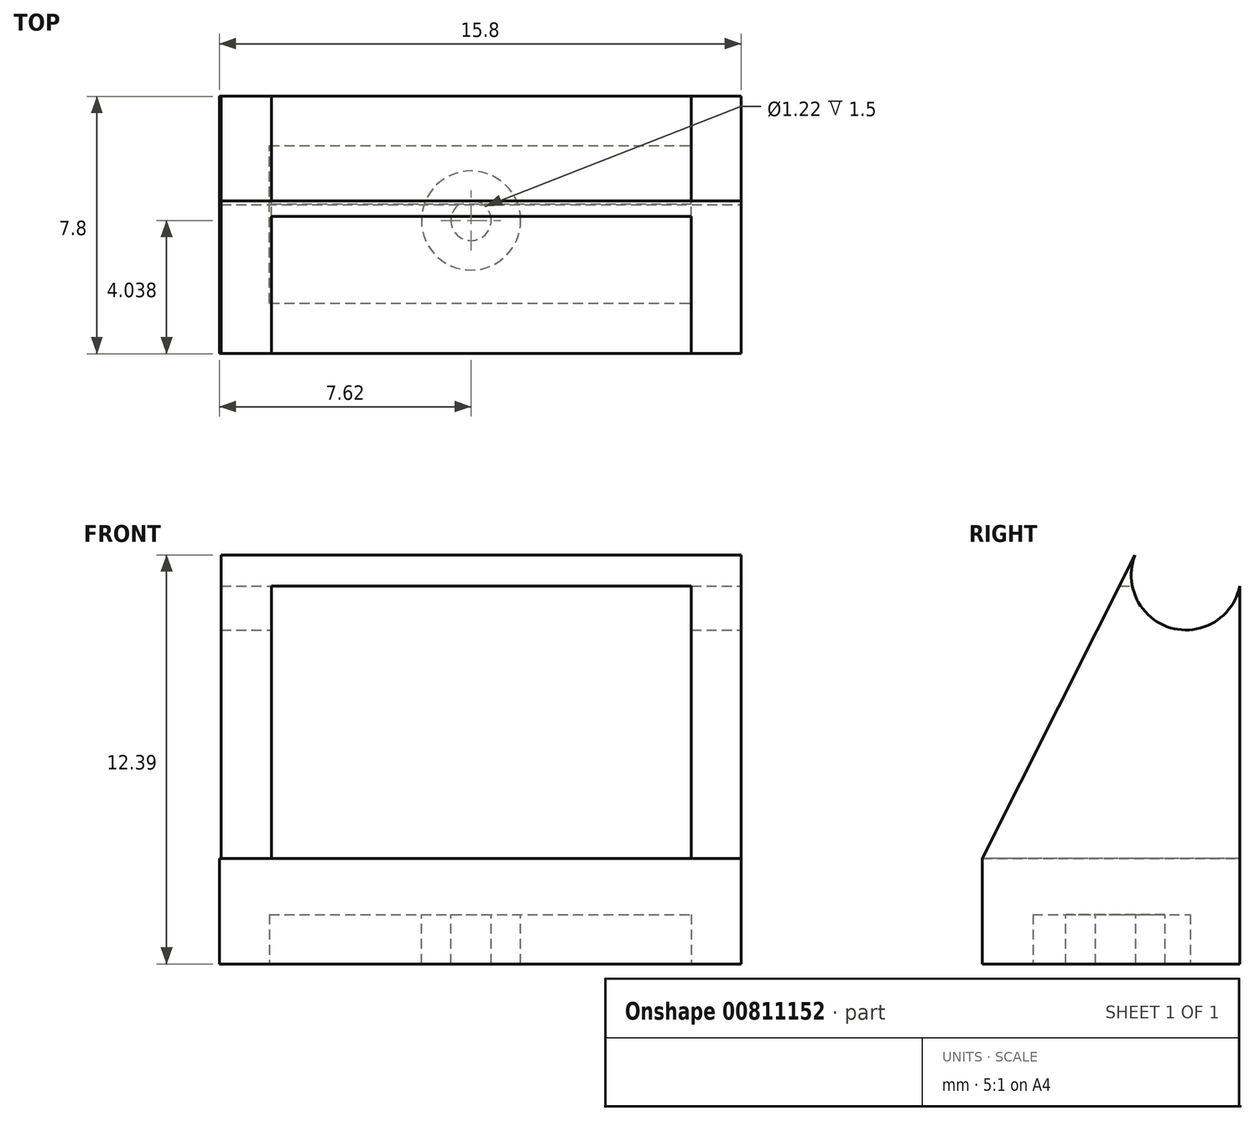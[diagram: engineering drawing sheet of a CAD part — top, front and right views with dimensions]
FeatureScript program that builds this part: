
annotation { "Feature Type Name" : "Feature", "Feature Type Description" : "" }
export const myFeature = defineFeature(function(context is Context, id is Id, definition is map)
    precondition{}
    {
        {
            var Q0;
            Q0=qCreatedBy(makeId("Top.planeOp"),FACE);
            var sketch = newSketch(context, id + "F0", { "sketchPlane" : qUnion([Q0])});
            skLineSegment(sketch, "E0.bottom", {"start": v(-8.33, 5.42) * mm, "end": v(7.47, 5.42) * mm});
            skLineSegment(sketch, "E0.top", {"start": v(-8.33, -2.38) * mm, "end": v(7.47, -2.38) * mm});
            skLineSegment(sketch, "E0.left", {"start": v(-8.33, 5.42) * mm, "end": v(-8.33, -2.38) * mm});
            skLineSegment(sketch, "E0.right", {"start": v(7.47, 5.42) * mm, "end": v(7.47, -2.38) * mm});
            skSolve(sketch);
        }
        {
            var Q0;
            Q0 = qSketchRegion(id + "F0", true);
            extrude(context, id + "F1", {"entities" : qUnion([Q0]), "depth" : 3.2 * mm, "offsetDistance" : 25 * mm});
        }
        {
            var Q0;
            Q0=makeQuery(id+"F1.opExtrude","CAP_FACE",FACE,{"disambiguationData":[OSD([sQuery(id+"F0.wireOp",EDGE,"E0.bottom"),sQuery(id+"F0.wireOp",EDGE,"E0.top"),sQuery(id+"F0.wireOp",EDGE,"E0.left"),sQuery(id+"F0.wireOp",EDGE,"E0.right")])],"isStart":true});
            var sketch = newSketch(context, id + "F2", { "sketchPlane" : qUnion([Q0])});
            skLineSegment(sketch, "E1", {"start": v(-8.33, -1.52) * mm, "end": v(-6.82, -1.52) * mm});
            skLineSegment(sketch, "E2", {"start": v(-0.87, 2.38) * mm, "end": v(-0.87, 0.84) * mm});
            skLineSegment(sketch, "E3", {"start": v(7.47, -1.52) * mm, "end": v(5.96, -1.52) * mm});
            skLineSegment(sketch, "E4", {"start": v(-0.43, -5.42) * mm, "end": v(-0.43, -3.93) * mm});
            skLineSegment(sketch, "E5.bottom", {"start": v(-6.82, 0.84) * mm, "end": v(5.96, 0.84) * mm});
            skLineSegment(sketch, "E5.top", {"start": v(-6.82, -3.93) * mm, "end": v(5.96, -3.93) * mm});
            skLineSegment(sketch, "E5.left", {"start": v(-6.82, 0.84) * mm, "end": v(-6.82, -3.93) * mm});
            skLineSegment(sketch, "E5.right", {"start": v(5.96, 0.84) * mm, "end": v(5.96, -3.93) * mm});
            skSolve(sketch);
        }
        {
            var Q0;
            Q0 = qSketchRegion(id + "F2", true);
            extrude(context, id + "F3", {"entities" : qUnion([Q0]), "operationType" : NewBodyOperationType.REMOVE, "oppositeDirection" : true, "depth" : 1.5 * mm, "offsetDistance" : 25 * mm});
        }
        {
            var Q0;
            Q0=makeQuery(id+"F3.boolean.opBoolean","COPY",FACE,{"derivedFrom":makeQuery(id+"F3.opExtrude","CAP_FACE",FACE,{"disambiguationData":[OSD([sQuery(id+"F2.wireOp",EDGE,"E5.bottom"),sQuery(id+"F2.wireOp",EDGE,"E5.top"),sQuery(id+"F2.wireOp",EDGE,"E5.left"),sQuery(id+"F2.wireOp",EDGE,"E5.right")])],"isStart":false})});
            var sketch = newSketch(context, id + "F4", { "sketchPlane" : qUnion([Q0])});
            skCircle(sketch, "E6", {"center": v(-0.7, -1.66) * mm, "radius": 0.6 * mm});
            skCircle(sketch, "E7", {"center": v(-0.7, -1.66) * mm, "radius": 1.5 * mm});
            skSolve(sketch);
        }
        {
            var Q0;
            Q0 = qSketchRegion(id + "F4", true);
            extrude(context, id + "F5", {"entities" : qUnion([Q0]), "operationType" : NewBodyOperationType.ADD, "depth" : 1.5 * mm, "offsetDistance" : 25 * mm});
        }
        {
            var Q0;
            Q0=makeQuery(id+"F1.opExtrude","SWEPT_FACE",FACE,{"disambiguationData":[OSD([sQuery(id+"F0.wireOp",EDGE,"E0.right")])]});
            var sketch = newSketch(context, id + "F6", { "sketchPlane" : qUnion([Q0])});
            skLineSegment(sketch, "E8", {"start": v(5.42, 3.2) * mm, "end": v(5.42, 11.78) * mm});
            skCircle(sketch, "E9", {"center": v(3.8, 11.78) * mm, "radius": 1.66 * mm});
            skLineSegment(sketch, "E10", {"start": v(2.38, 12.66) * mm, "end": v(-2.38, 3.2) * mm});
            skSolve(sketch);
        }
        {
            var Q0;
            {var subQ1=sQuery(id+"F0.wireOp",EDGE,"E0.right");var subQ2=makeQuery(id+"F1.opExtrude","CAP_EDGE",EDGE,{"disambiguationData":[OSD([subQ1])],"isStart":false});Q0=makeQuery(id+"F6.imprint","IMPRINT",FACE,{"disambiguationData":[TD([[makeQuery(id+"F6.imprint","IMPRINT",EDGE,{"derivedFrom":subQ2}),-1.0]])]});}
            extrude(context, id + "F7", {"entities" : qUnion([Q0]), "operationType" : NewBodyOperationType.ADD, "oppositeDirection" : true, "depth" : 15.75 * mm, "offsetDistance" : 25 * mm});
        }
        {
            var Q0;
            Q0=sQuery(id+"F6.wireOp",EDGE,"E9");
            extrude(context, id + "F8", {"bodyType" : ToolBodyType.SURFACE, "surfaceEntities" : qUnion([Q0]), "oppositeDirection" : true, "depth" : 15.75 * mm, "offsetDistance" : 25 * mm});
        }
        {
            var Q0;
            Q0=makeQuery(id+"F7.boolean.opBoolean","MERGE",FACE,{"derivedFrom":[makeQuery(id+"F1.opExtrude","SWEPT_FACE",FACE,{"disambiguationData":[OSD([sQuery(id+"F0.wireOp",EDGE,"E0.bottom")])]}),makeQuery(id+"F7.opExtrude","SWEPT_FACE",FACE,{"disambiguationData":[OSD([sQuery(id+"F6.wireOp",EDGE,"E8")])]})]});
            var sketch = newSketch(context, id + "F9", { "sketchPlane" : qUnion([Q0])});
            skLineSegment(sketch, "E11", {"start": v(-7.47, 3.21) * mm, "end": v(8.33, 3.2) * mm});
            skLineSegment(sketch, "E12", {"start": v(-5.96, 11.46) * mm, "end": v(-5.96, 3.21) * mm});
            skLineSegment(sketch, "E13", {"start": v(6.75, 11.46) * mm, "end": v(6.75, 3.2) * mm});
            skPoint(sketch, "E14.end.orphan", {"position": v(-5.96, 4.72) * mm});
            skPoint(sketch, "E15.end.orphan", {"position": v(6.75, 4.72) * mm});
            skPoint(sketch, "E15.start.orphan", {"position": v(8.28, 4.72) * mm});
            skSolve(sketch);
        }
        {
            var Q0;
            Q0 = qSketchRegion(id + "F9", true);
            var Q1;
            {var subQ0=sQuery(id+"F9.wireOp",EDGE,"E12");Q1=makeQuery(id+"F9.imprint","IMPRINT",FACE,{"disambiguationData":[TD([[makeQuery(id+"F9.imprint","IMPRINT",EDGE,{"derivedFrom":subQ0}),1.0]])]});}
            extrude(context, id + "F10", {"entities" : qUnion([Q0, Q1]), "operationType" : NewBodyOperationType.REMOVE, "oppositeDirection" : true, "depth" : 25 * mm, "offsetDistance" : 25 * mm});
        }
    });
